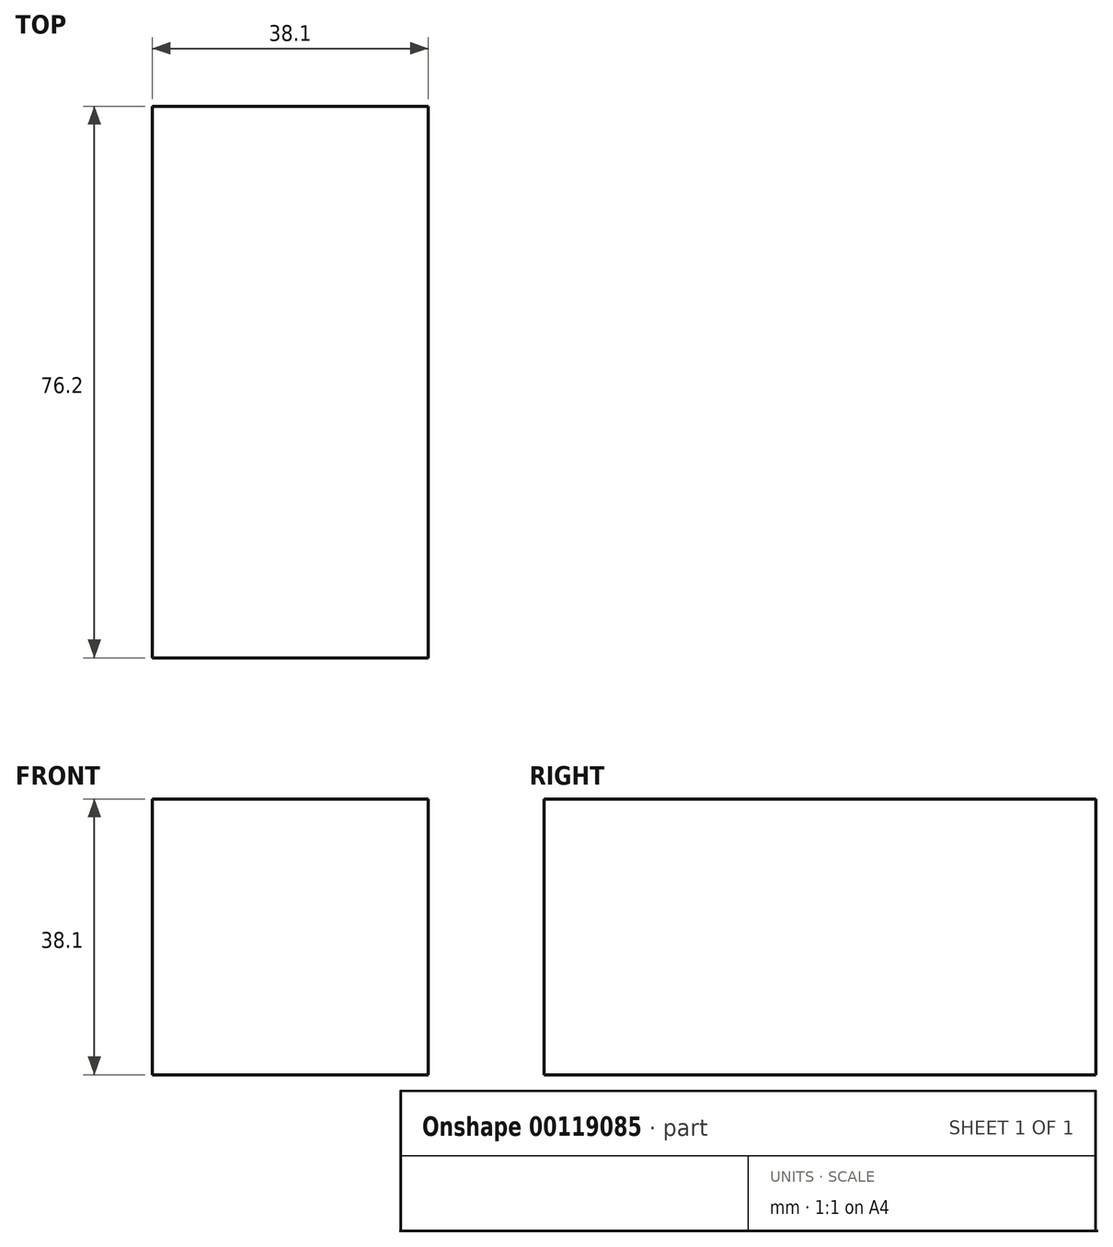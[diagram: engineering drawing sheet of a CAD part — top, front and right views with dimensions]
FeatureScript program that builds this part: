
annotation { "Feature Type Name" : "Feature", "Feature Type Description" : "" }
export const myFeature = defineFeature(function(context is Context, id is Id, definition is map)
    precondition{}
    {
        {
            var Q0;
            Q0=qCreatedBy(makeId("Front.planeOp"),FACE);
            var sketch = newSketch(context, id + "F0", { "sketchPlane" : qUnion([Q0])});
            skLineSegment(sketch, "E0.bottom", {"start": v(0, 0) * mm, "end": v(38.1, 0) * mm});
            skLineSegment(sketch, "E0.top", {"start": v(0, 38.1) * mm, "end": v(38.1, 38.1) * mm});
            skLineSegment(sketch, "E0.left", {"start": v(0, 0) * mm, "end": v(0, 38.1) * mm});
            skLineSegment(sketch, "E0.right", {"start": v(38.1, 0) * mm, "end": v(38.1, 38.1) * mm});
            skSolve(sketch);
        }
        {
            var Q0;
            Q0=makeQuery(id+"F0.imprint","IMPRINT",FACE,{"disambiguationData":[TD([[makeQuery(id+"F0.imprint","IMPRINT",EDGE,{"derivedFrom":sQuery(id+"F0.wireOp",EDGE,"E0.bottom")}),1.0]])]});
            extrude(context, id + "F1", {"entities" : qUnion([Q0]), "oppositeDirection" : true, "depth" : 76.2 * mm});
        }
    });
